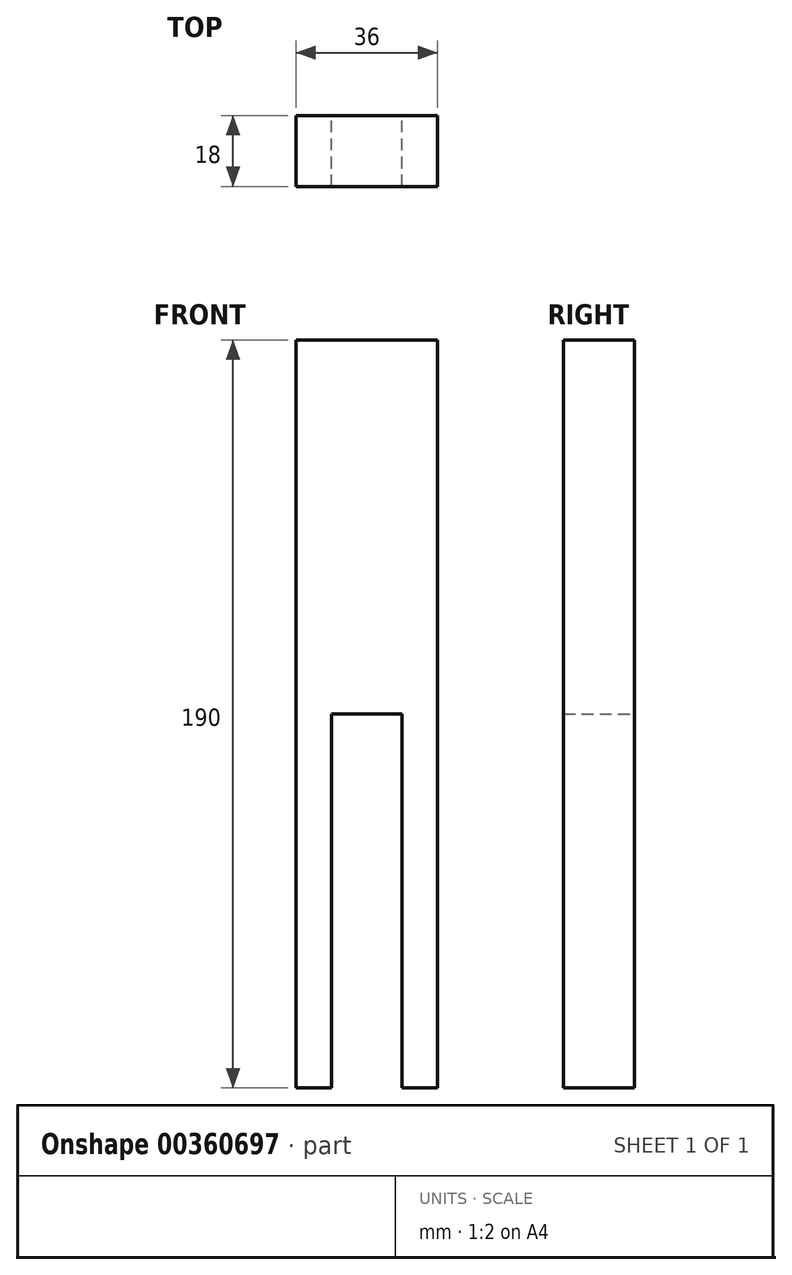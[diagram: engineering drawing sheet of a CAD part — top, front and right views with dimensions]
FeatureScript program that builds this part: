
annotation { "Feature Type Name" : "Feature", "Feature Type Description" : "" }
export const myFeature = defineFeature(function(context is Context, id is Id, definition is map)
    precondition{}
    {
        {
            var Q0;
            Q0=qCreatedBy(makeId("Front.planeOp"),FACE);
            var sketch = newSketch(context, id + "F0", { "sketchPlane" : qUnion([Q0])});
            skLineSegment(sketch, "E0.bottom", {"start": v(-18, 0) * mm, "end": v(-9, 0) * mm});
            skLineSegment(sketch, "E0.top", {"start": v(-18, 190) * mm, "end": v(18, 190) * mm});
            skLineSegment(sketch, "E0.left", {"start": v(-18, 0) * mm, "end": v(-18, 190) * mm});
            skLineSegment(sketch, "E0.right", {"start": v(18, 0) * mm, "end": v(18, 190) * mm});
            skLineSegment(sketch, "E1.top", {"start": v(-9, 95) * mm, "end": v(9, 95) * mm});
            skLineSegment(sketch, "E1.left", {"start": v(-9, 0) * mm, "end": v(-9, 95) * mm});
            skLineSegment(sketch, "E1.right", {"start": v(9, 0) * mm, "end": v(9, 95) * mm});
            skLineSegment(sketch, "E2.trimOffspring", {"start": v(9, 0) * mm, "end": v(18, 0) * mm});
            skSolve(sketch);
        }
        {
            var Q0;
            Q0=makeQuery(id+"F0.imprint","IMPRINT",FACE,{"disambiguationData":[TD([[makeQuery(id+"F0.imprint","IMPRINT",EDGE,{"derivedFrom":sQuery(id+"F0.wireOp",EDGE,"E0.bottom")}),1.0]])]});
            extrude(context, id + "F1", {"entities" : qUnion([Q0]), "depth" : 18 * mm});
        }
    });
